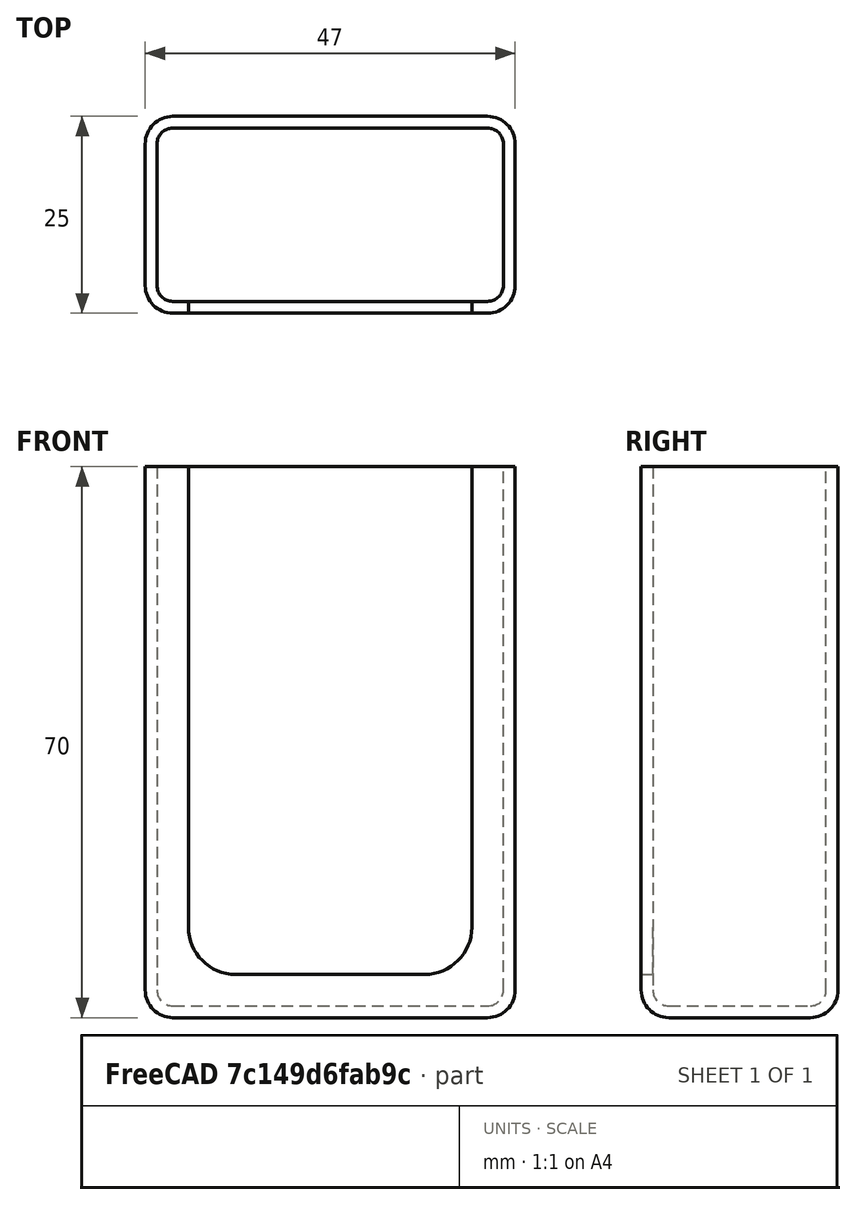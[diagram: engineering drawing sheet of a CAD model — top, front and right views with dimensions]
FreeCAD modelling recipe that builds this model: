
FCSTD DOCUMENT  (FreeCAD 1.0R39109 (Git))
Label: FilipKutija
License: All rights reserved
LicenseURL: https://en.wikipedia.org/wiki/All_rights_reserved
objects: Part::Fillet×5, Part::Box×3, Part::MultiFuse×1, Part::Cut×1
note: 10 computed .brp shape members not serialized (recipe doc carries the construction recipe); baked Part::Feature solids carry a one-line shape summary decoded from their .brp

FEATURE [Part::Box] Box  label="Cube"
  AttacherType = Attacher::AttachEngine3D
  Height = 70
  Length = 44
  Placement = pos=(-22,0,0) rot=(0,0,1;0rad)
  Width = 22
FEATURE [Part::Box] Box002  label="Cube002"
  AttacherType = Attacher::AttachEngine3D
  Height = 70
  Length = 36
  Placement = pos=(-18,-10,4) rot=(0,0,1;0rad)
  Width = 20.5
FEATURE [Part::Fillet] Fillet004
  Base = -> Box002
  EdgeLinks = -> Box002 [Edge4,Edge8]
  Edges = 2 edges r=6: [Edge4,Edge8]
FEATURE [Part::Fillet] Fillet
  Base = -> Box
  EdgeLinks = -> Box [Edge4,Edge8]
  Edges = 2 edges r=2: [Edge4,Edge8]
FEATURE [Part::Fillet] Fillet005
  Base = -> Fillet
  EdgeLinks = -> Fillet [Edge8,Edge16]
  Edges = 2 edges r=2: [Edge8,Edge16]
FEATURE [Part::Box] Box003  label="Cube003"
  AttacherType = Attacher::AttachEngine3D
  Height = 70
  Length = 47
  Placement = pos=(-23.5,-1.5,-1.5) rot=(0,0,1;0rad)
  Width = 25
FEATURE [Part::Fillet] Fillet006
  Base = -> Box003
  EdgeLinks = -> Box003 [Edge4,Edge8]
  Edges = 2 edges r=3.5: [Edge4,Edge8]
FEATURE [Part::Fillet] Fillet007
  Base = -> Fillet006
  EdgeLinks = -> Fillet006 [Edge5,Edge14]
  Edges = 2 edges r=3.5: [Edge5,Edge14]
FEATURE [Part::MultiFuse] Fusion
  Shapes = -> [Fillet005,Fillet004]
FEATURE [Part::Cut] Cut
  Base = -> Fillet007
  Tool = -> Fusion
